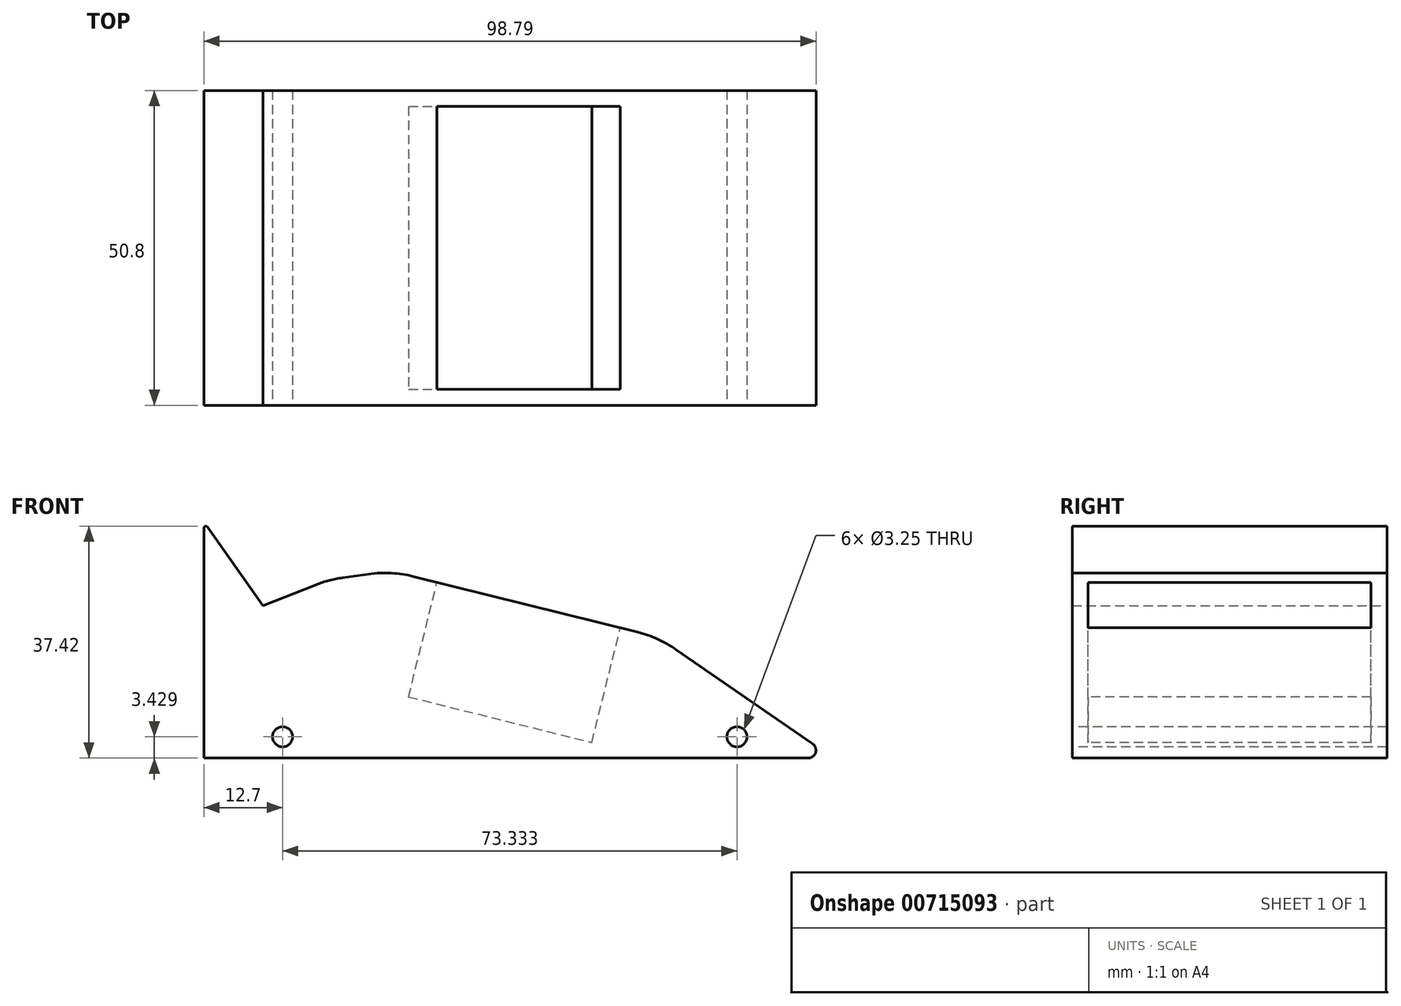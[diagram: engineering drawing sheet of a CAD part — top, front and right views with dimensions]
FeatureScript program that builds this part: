
annotation { "Feature Type Name" : "Feature", "Feature Type Description" : "" }
export const myFeature = defineFeature(function(context is Context, id is Id, definition is map)
    precondition{}
    {
        {
            var Q0;
            Q0=qCreatedBy(makeId("Front.planeOp"),FACE);
            var sketch = newSketch(context, id + "F0", { "sketchPlane" : qUnion([Q0])});
            skLineSegment(sketch, "E0.bottom", {"start": v(0, 0) * mm, "end": v(101.6, 0) * mm});
            skLineSegment(sketch, "E0.top", {"start": v(0, 38.1) * mm, "end": v(101.6, 38.1) * mm});
            skLineSegment(sketch, "E0.left", {"start": v(0, 0) * mm, "end": v(0, 38.1) * mm});
            skLineSegment(sketch, "E0.right", {"start": v(101.6, 0) * mm, "end": v(101.6, 38.1) * mm});
            skLineSegment(sketch, "E1", {"start": v(9.53, 24.61) * mm, "end": v(20.17, 28.78) * mm});
            skLineSegment(sketch, "E2", {"start": v(20.17, 28.78) * mm, "end": v(30.24, 30.2) * mm});
            skLineSegment(sketch, "E3", {"start": v(30.24, 30.2) * mm, "end": v(73.37, 19.46) * mm});
            skLineSegment(sketch, "E4", {"start": v(73.37, 19.46) * mm, "end": v(101.6, 0) * mm});
            skLineSegment(sketch, "E5", {"start": v(0, 38.1) * mm, "end": v(0, 0) * mm});
            skLineSegment(sketch, "E6", {"start": v(9.53, 24.61) * mm, "end": v(0, 38.1) * mm});
            skSolve(sketch);
        }
        {
            var Q0;
            Q0=makeQuery(id+"F0.imprint","IMPRINT",FACE,{"disambiguationData":[TD([[makeQuery(id+"F0.imprint","IMPRINT",EDGE,{"derivedFrom":sQuery(id+"F0.wireOp",EDGE,"E1")}),-1.0]])]});
            extrude(context, id + "F1", {"entities" : qUnion([Q0]), "depth" : 50.8 * mm, "offsetDistance" : 25.4 * mm});
        }
        {
            var Q0;
            Q0=makeQuery(id+"F1.opExtrude","SWEPT_EDGE",EDGE,{"disambiguationData":[OSD([sQuery(id+"F0.wireOp",EDGE,"E2"),sQuery(id+"F0.wireOp",EDGE,"E3")])]});
            var Q1;
            Q1=makeQuery(id+"F1.opExtrude","SWEPT_EDGE",EDGE,{"disambiguationData":[OSD([sQuery(id+"F0.wireOp",EDGE,"E3"),sQuery(id+"F0.wireOp",EDGE,"E4")])]});
            var Q2;
            Q2=makeQuery(id+"F1.opExtrude","SWEPT_EDGE",EDGE,{"disambiguationData":[OSD([sQuery(id+"F0.wireOp",EDGE,"E1"),sQuery(id+"F0.wireOp",EDGE,"E2")])]});
            fillet(context, id + "F2", {"entities" : qUnion([Q0, Q1, Q2]), "radius" : 19.05 * mm, "tangentPropagation" : true, "allowEdgeOverflow" : false});
        }
        {
            var Q0;
            Q0=makeQuery(id+"F1.opExtrude","SWEPT_EDGE",EDGE,{"disambiguationData":[OSD([sQuery(id+"F0.wireOp",EDGE,"E0.right"),sQuery(id+"F0.wireOp",EDGE,"E4"),sQuery(id+"F0.wireOp",EDGE,"E0.bottom")])]});
            fillet(context, id + "F3", {"entities" : qUnion([Q0]), "radius" : 1.27 * mm, "tangentPropagation" : true, "allowEdgeOverflow" : false});
        }
        {
            var Q0;
            Q0=makeQuery(id+"F1.opExtrude","SWEPT_FACE",FACE,{"disambiguationData":[OSD([sQuery(id+"F0.wireOp",EDGE,"E3")])]});
            var sketch = newSketch(context, id + "F4", { "sketchPlane" : qUnion([Q0])});
            skLineSegment(sketch, "E7.bottom", {"start": v(29.67, -2.57) * mm, "end": v(60.15, -2.57) * mm});
            skLineSegment(sketch, "E7.top", {"start": v(29.67, -48.23) * mm, "end": v(60.15, -48.23) * mm});
            skLineSegment(sketch, "E7.left", {"start": v(29.67, -2.57) * mm, "end": v(29.67, -48.23) * mm});
            skLineSegment(sketch, "E7.right", {"start": v(60.15, -2.57) * mm, "end": v(60.15, -48.23) * mm});
            skSolve(sketch);
        }
        {
            var Q0;
            Q0 = qSketchRegion(id + "F4", true);
            extrude(context, id + "F5", {"entities" : qUnion([Q0]), "operationType" : NewBodyOperationType.REMOVE, "oppositeDirection" : true, "depth" : 19.05 * mm, "offsetDistance" : 25.4 * mm});
        }
        {
            var Q0;
            Q0=makeQuery(id+"F1.opExtrude","CAP_FACE",FACE,{"disambiguationData":[OSD([sQuery(id+"F0.wireOp",EDGE,"E1"),sQuery(id+"F0.wireOp",EDGE,"E2"),sQuery(id+"F0.wireOp",EDGE,"E3"),sQuery(id+"F0.wireOp",EDGE,"E4"),sQuery(id+"F0.wireOp",EDGE,"E0.bottom"),sQuery(id+"F0.wireOp",EDGE,"E5"),sQuery(id+"F0.wireOp",EDGE,"F37g2EBu-W4Ht-WV8g-5x4N-K7N5xmxNQfkF")])],"isStart":false});
            var sketch = newSketch(context, id + "F6", { "sketchPlane" : qUnion([Q0])});
            skPoint(sketch, "E8", {"position": v(12.7, 3.43) * mm});
            skPoint(sketch, "E9", {"position": v(86.03, 3.43) * mm});
            skSolve(sketch);
        }
        {
            var Q0;
            Q0=sQuery(id+"F6.wireOp",VERTEX,"E8");
            var Q1;
            Q1=sQuery(id+"F6.wireOp",VERTEX,"E9");
            var Q2;
            Q2=makeQuery(id+"F1.opExtrude","SWEPT_BODY",BODY,{"disambiguationData":[OSD([sQuery(id+"F0.wireOp",EDGE,"E1"),sQuery(id+"F0.wireOp",EDGE,"E2"),sQuery(id+"F0.wireOp",EDGE,"E3"),sQuery(id+"F0.wireOp",EDGE,"E4"),sQuery(id+"F0.wireOp",EDGE,"E0.bottom"),sQuery(id+"F0.wireOp",EDGE,"E5"),sQuery(id+"F0.wireOp",EDGE,"F37g2EBu-W4Ht-WV8g-5x4N-K7N5xmxNQfkF")])]});
            hole(context, id + "F7", {"style" : HoleStyle.SIMPLE, "endStyle" : HoleEndStyle.THROUGH, "holeDiameter" : 3.25 * mm, "majorDiameter" : 6.35 * mm, "isTappedThrough" : true, "tappedDepth" : 12.7 * mm, "tapClearance" : 3, "locations" : qUnion([Q0, Q1]), "scope" : qUnion([Q2])});
        }
        {
            var Q0;
            Q0=makeQuery(id+"F1.opExtrude","SWEPT_EDGE",EDGE,{"disambiguationData":[OSD([sQuery(id+"F0.wireOp",EDGE,"E0.top"),sQuery(id+"F0.wireOp",EDGE,"E5"),sQuery(id+"F0.wireOp",EDGE,"E6")])]});
            fillet(context, id + "F8", {"entities" : qUnion([Q0]), "radius" : 0.32 * mm, "tangentPropagation" : true, "allowEdgeOverflow" : false});
        }
    });
